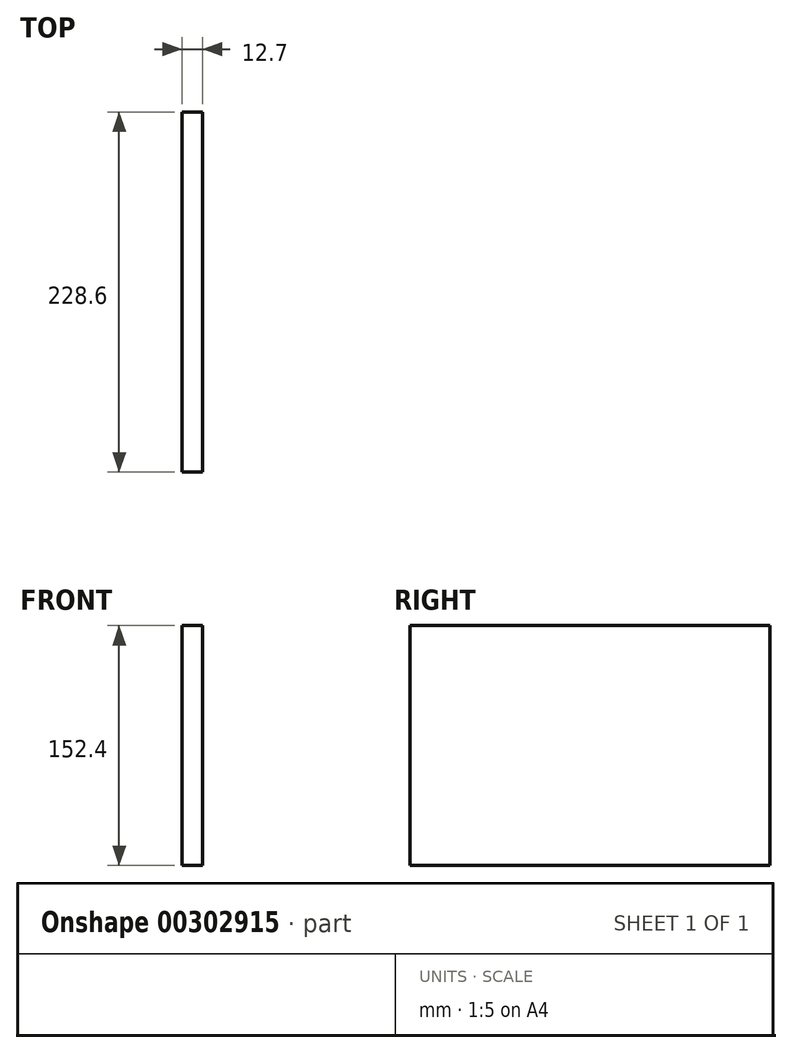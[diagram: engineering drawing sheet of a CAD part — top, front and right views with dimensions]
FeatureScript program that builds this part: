
annotation { "Feature Type Name" : "Feature", "Feature Type Description" : "" }
export const myFeature = defineFeature(function(context is Context, id is Id, definition is map)
    precondition{}
    {
        {
            var Q0;
            Q0=qCreatedBy(makeId("Right.planeOp"),FACE);
            var sketch = newSketch(context, id + "F0", { "sketchPlane" : qUnion([Q0])});
            skLineSegment(sketch, "E0.bottom", {"start": v(114.3, 76.2) * mm, "end": v(-114.3, 76.2) * mm});
            skLineSegment(sketch, "E0.top", {"start": v(114.3, -76.2) * mm, "end": v(-114.3, -76.2) * mm});
            skLineSegment(sketch, "E0.left", {"start": v(114.3, 76.2) * mm, "end": v(114.3, -76.2) * mm});
            skLineSegment(sketch, "E0.right", {"start": v(-114.3, 76.2) * mm, "end": v(-114.3, -76.2) * mm});
            skPoint(sketch, "E0.middle", {"position": v(0, 0) * mm});
            skSolve(sketch);
        }
        {
            var Q0;
            Q0=makeQuery(id+"F0.imprint","IMPRINT",FACE,{"disambiguationData":[TD([[makeQuery(id+"F0.imprint","IMPRINT",EDGE,{"derivedFrom":sQuery(id+"F0.wireOp",EDGE,"E0.bottom")}),1.0]])]});
            extrude(context, id + "F1", {"entities" : qUnion([Q0]), "depth" : 12.7 * mm});
        }
    });
